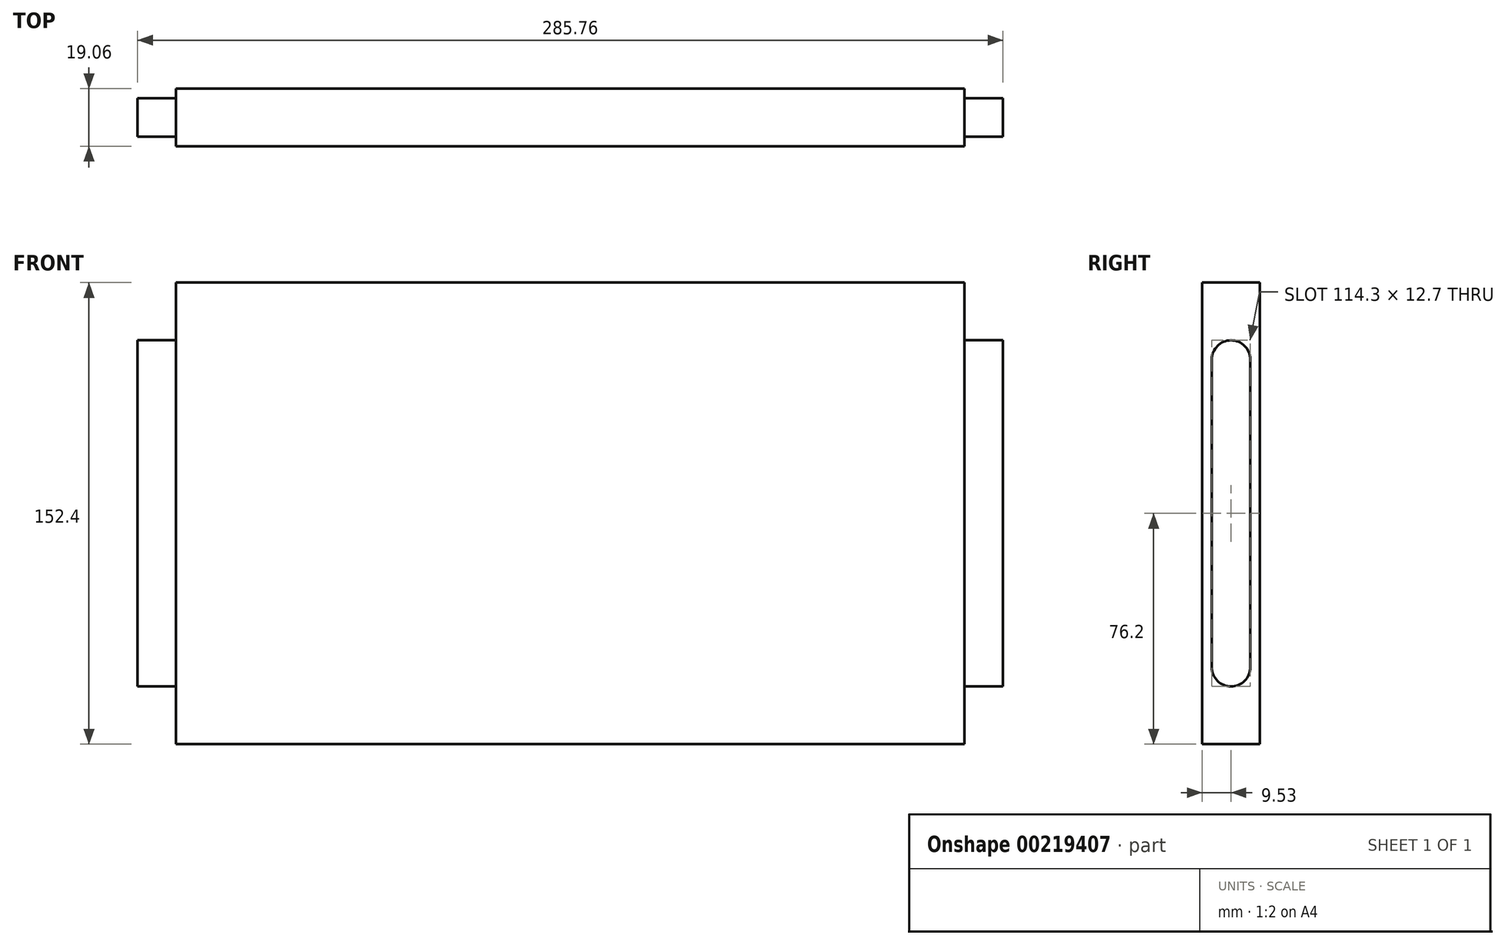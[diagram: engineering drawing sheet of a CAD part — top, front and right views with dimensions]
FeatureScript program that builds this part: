
annotation { "Feature Type Name" : "Feature", "Feature Type Description" : "" }
export const myFeature = defineFeature(function(context is Context, id is Id, definition is map)
    precondition{}
    {
        {
            var Q0;
            Q0=qCreatedBy(makeId("Top.planeOp"),FACE);
            var sketch = newSketch(context, id + "F0", { "sketchPlane" : qUnion([Q0])});
            skLineSegment(sketch, "E0.bottom", {"start": v(130.18, -9.52) * mm, "end": v(-130.18, -9.53) * mm});
            skLineSegment(sketch, "E0.top", {"start": v(130.18, 9.53) * mm, "end": v(-130.18, 9.52) * mm});
            skLineSegment(sketch, "E0.left", {"start": v(130.18, -9.52) * mm, "end": v(130.18, 9.53) * mm});
            skLineSegment(sketch, "E0.right", {"start": v(-130.18, -9.53) * mm, "end": v(-130.18, 9.53) * mm});
            skPoint(sketch, "E0.middle", {"position": v(0, 0) * mm});
            skSolve(sketch);
        }
        {
            var Q0;
            Q0=makeQuery(id+"F0.imprint","IMPRINT",FACE,{"disambiguationData":[TD([[makeQuery(id+"F0.imprint","IMPRINT",EDGE,{"derivedFrom":sQuery(id+"F0.wireOp",EDGE,"E0.bottom")}),-1.0]])]});
            extrude(context, id + "F1", {"entities" : qUnion([Q0]), "oppositeDirection" : true, "depth" : 152.4 * mm, "offsetDistance" : 25.4 * mm});
        }
        {
            var Q0;
            Q0=makeQuery(id+"F1.opExtrude","SWEPT_FACE",FACE,{"disambiguationData":[OSD([sQuery(id+"F0.wireOp",EDGE,"E0.right")])]});
            var sketch = newSketch(context, id + "F2", { "sketchPlane" : qUnion([Q0])});
            skLineSegment(sketch, "E1.bottom", {"start": v(-6.35, -133.35) * mm, "end": v(6.35, -133.35) * mm});
            skLineSegment(sketch, "E1.top", {"start": v(-6.35, -19.05) * mm, "end": v(6.35, -19.05) * mm});
            skLineSegment(sketch, "E1.left", {"start": v(-6.35, -133.35) * mm, "end": v(-6.35, -19.05) * mm});
            skLineSegment(sketch, "E1.right", {"start": v(6.35, -133.35) * mm, "end": v(6.35, -19.05) * mm});
            skPoint(sketch, "E1.middle", {"position": v(0, -76.2) * mm});
            skSolve(sketch);
        }
        {
            var Q0;
            Q0=makeQuery(id+"F2.imprint","IMPRINT",FACE,{"disambiguationData":[TD([[makeQuery(id+"F2.imprint","IMPRINT",EDGE,{"derivedFrom":sQuery(id+"F2.wireOp",EDGE,"E1.bottom")}),1.0]])]});
            extrude(context, id + "F3", {"entities" : qUnion([Q0]), "operationType" : NewBodyOperationType.ADD, "depth" : 12.7 * mm, "offsetDistance" : 25.4 * mm});
        }
        {
            var Q0;
            Q0=makeQuery(id+"F3.opExtrude","SWEPT_EDGE",EDGE,{"disambiguationData":[OSD([sQuery(id+"F2.wireOp",EDGE,"E1.top"),sQuery(id+"F2.wireOp",EDGE,"E1.left")])]});
            var Q1;
            Q1=makeQuery(id+"F3.opExtrude","SWEPT_EDGE",EDGE,{"disambiguationData":[OSD([sQuery(id+"F2.wireOp",EDGE,"E1.top"),sQuery(id+"F2.wireOp",EDGE,"E1.right")])]});
            var Q2;
            Q2=makeQuery(id+"F3.opExtrude","SWEPT_EDGE",EDGE,{"disambiguationData":[OSD([sQuery(id+"F2.wireOp",EDGE,"E1.bottom"),sQuery(id+"F2.wireOp",EDGE,"E1.right")])]});
            var Q3;
            Q3=makeQuery(id+"F3.opExtrude","SWEPT_EDGE",EDGE,{"disambiguationData":[OSD([sQuery(id+"F2.wireOp",EDGE,"E1.bottom"),sQuery(id+"F2.wireOp",EDGE,"E1.left")])]});
            fillet(context, id + "F4", {"entities" : qUnion([Q0, Q1, Q2, Q3]), "radius" : 6.35 * mm, "tangentPropagation" : true, "allowEdgeOverflow" : false});
        }
        {
            var Q0;
            Q0=makeQuery(id+"F1.opExtrude","SWEPT_FACE",FACE,{"disambiguationData":[OSD([sQuery(id+"F0.wireOp",EDGE,"E0.left")])]});
            var sketch = newSketch(context, id + "F5", { "sketchPlane" : qUnion([Q0])});
            skLineSegment(sketch, "E2.bottom", {"start": v(-6.35, -133.35) * mm, "end": v(6.35, -133.35) * mm});
            skLineSegment(sketch, "E2.top", {"start": v(-6.35, -19.05) * mm, "end": v(6.35, -19.05) * mm});
            skLineSegment(sketch, "E2.left", {"start": v(-6.35, -133.35) * mm, "end": v(-6.35, -19.05) * mm});
            skLineSegment(sketch, "E2.right", {"start": v(6.35, -133.35) * mm, "end": v(6.35, -19.05) * mm});
            skPoint(sketch, "E2.middle", {"position": v(0, -76.2) * mm});
            skSolve(sketch);
        }
        {
            var Q0;
            Q0=makeQuery(id+"F5.imprint","IMPRINT",FACE,{"disambiguationData":[TD([[makeQuery(id+"F5.imprint","IMPRINT",EDGE,{"derivedFrom":sQuery(id+"F5.wireOp",EDGE,"E2.bottom")}),1.0]])]});
            extrude(context, id + "F6", {"entities" : qUnion([Q0]), "operationType" : NewBodyOperationType.ADD, "depth" : 12.7 * mm, "offsetDistance" : 25.4 * mm});
        }
        {
            var Q0;
            Q0=makeQuery(id+"F6.opExtrude","SWEPT_EDGE",EDGE,{"disambiguationData":[OSD([sQuery(id+"F5.wireOp",EDGE,"E2.top"),sQuery(id+"F5.wireOp",EDGE,"E2.left")])]});
            var Q1;
            Q1=makeQuery(id+"F6.opExtrude","SWEPT_EDGE",EDGE,{"disambiguationData":[OSD([sQuery(id+"F5.wireOp",EDGE,"E2.top"),sQuery(id+"F5.wireOp",EDGE,"E2.right")])]});
            var Q2;
            Q2=makeQuery(id+"F6.opExtrude","SWEPT_EDGE",EDGE,{"disambiguationData":[OSD([sQuery(id+"F5.wireOp",EDGE,"E2.bottom"),sQuery(id+"F5.wireOp",EDGE,"E2.right")])]});
            var Q3;
            Q3=makeQuery(id+"F6.opExtrude","SWEPT_EDGE",EDGE,{"disambiguationData":[OSD([sQuery(id+"F5.wireOp",EDGE,"E2.bottom"),sQuery(id+"F5.wireOp",EDGE,"E2.left")])]});
            fillet(context, id + "F7", {"entities" : qUnion([Q0, Q1, Q2, Q3]), "radius" : 6.35 * mm, "tangentPropagation" : true, "allowEdgeOverflow" : false});
        }
    });
